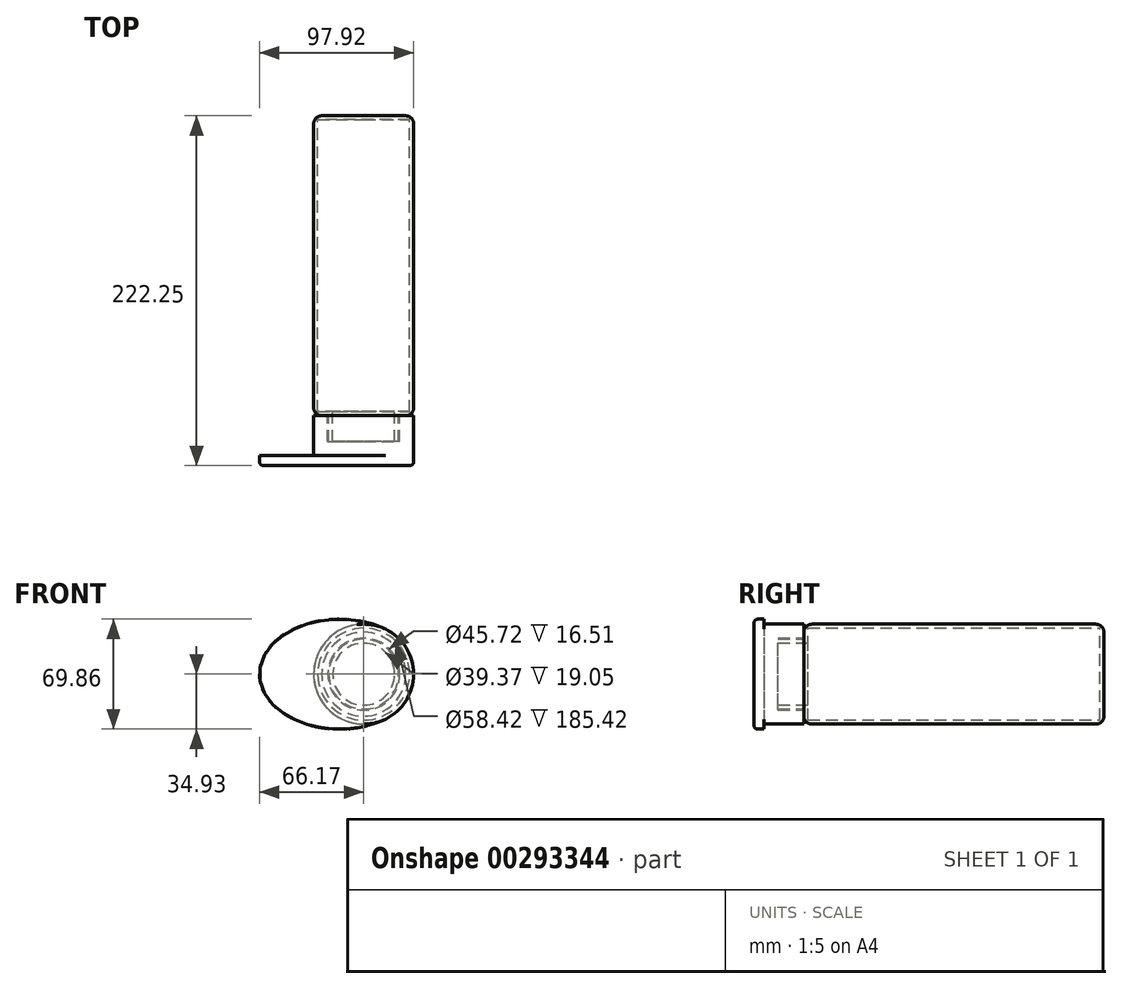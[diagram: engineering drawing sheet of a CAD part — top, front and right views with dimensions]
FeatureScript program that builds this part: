
annotation { "Feature Type Name" : "Feature", "Feature Type Description" : "" }
export const myFeature = defineFeature(function(context is Context, id is Id, definition is map)
    precondition{}
    {
        {
            var Q0;
            Q0=qCreatedBy(makeId("Front.planeOp"),FACE);
            var sketch = newSketch(context, id + "F0", { "sketchPlane" : qUnion([Q0])});
            skCircle(sketch, "E0", {"center": v(0, 0) * mm, "radius": 31.75 * mm});
            skSolve(sketch);
        }
        {
            var Q0;
            Q0 = qSketchRegion(id + "F0", true);
            extrude(context, id + "F1", {"entities" : qUnion([Q0]), "depth" : 190.5 * mm});
        }
        {
            var Q0;
            Q0=makeQuery(id+"F1.opExtrude","CAP_FACE",FACE,{"disambiguationData":[OSD([sQuery(id+"F0.wireOp",EDGE,"E0")])],"isStart":false});
            var sketch = newSketch(context, id + "F2", { "sketchPlane" : qUnion([Q0])});
            skCircle(sketch, "E1", {"center": v(0, 0) * mm, "radius": 22.23 * mm});
            skSolve(sketch);
        }
        {
            var Q0;
            Q0 = qSketchRegion(id + "F2", true);
            extrude(context, id + "F3", {"entities" : qUnion([Q0]), "operationType" : NewBodyOperationType.ADD, "depth" : 25.4 * mm});
        }
        {
            var Q0;
            Q0=makeQuery(id+"F3.opExtrude","CAP_FACE",FACE,{"disambiguationData":[OSD([sQuery(id+"F2.wireOp",EDGE,"E1")])],"isStart":false});
            shell(context, id + "F4", {"entities" : qUnion([Q0]), "thickness" : 2.54 * mm});
        }
        {
            var Q0;
            Q0=makeQuery(id+"F1.opExtrude","CAP_EDGE",EDGE,{"disambiguationData":[OSD([sQuery(id+"F0.wireOp",EDGE,"E0")])],"isStart":false});
            var Q1;
            Q1=makeQuery(id+"F1.opExtrude","CAP_EDGE",EDGE,{"disambiguationData":[OSD([sQuery(id+"F0.wireOp",EDGE,"E0")])],"isStart":true});
            fillet(context, id + "F5", {"entities" : qUnion([Q0, Q1]), "radius" : 5.08 * mm, "tangentPropagation" : true, "allowEdgeOverflow" : false});
        }
        {
            var Q0;
            Q0=makeQuery(id+"F1.opExtrude","CAP_FACE",FACE,{"disambiguationData":[OSD([sQuery(id+"F0.wireOp",EDGE,"E0")])],"isStart":false});
            var sketch = newSketch(context, id + "F6", { "sketchPlane" : qUnion([Q0])});
            skCircle(sketch, "E2", {"center": v(0, 0) * mm, "radius": 31.75 * mm});
            skSolve(sketch);
        }
        {
            var Q0;
            Q0 = qSketchRegion(id + "F6", true);
            extrude(context, id + "F7", {"entities" : qUnion([Q0]), "depth" : 25.4 * mm});
        }
        {
            var Q0;
            Q0=makeQuery(id+"F7.opExtrude","CAP_FACE",FACE,{"disambiguationData":[OSD([sQuery(id+"F6.wireOp",EDGE,"E2")])],"isStart":true});
            shell(context, id + "F8", {"entities" : qUnion([Q0]), "thickness" : 8.9 * mm});
        }
        {
            var Q0;
            Q0=makeQuery(id+"F7.opExtrude","CAP_FACE",FACE,{"disambiguationData":[OSD([sQuery(id+"F6.wireOp",EDGE,"E2")])],"isStart":false});
            var sketch = newSketch(context, id + "F9", { "sketchPlane" : qUnion([Q0])});
            skArc(sketch, "E3", {"start": v(13.77, -28.6) * mm, "mid": v(31.75, 0) * mm, "end": v(13.77, 28.6) * mm});
            skEllipticalArc(sketch, "E4", {});
            skFitSpline(sketch, "E5.0", {"points": [v(27.78, -1.18) * mm, v(27.83, 0) * mm, v(27.78, 1.18) * mm, v(27.61, 2.76) * mm, v(27.19, 4.72) * mm, v(26.33, 7.08) * mm, v(25.1, 9.44) * mm, v(23.5, 11.78) * mm, v(21.5, 14.08) * mm, v(19.5, 15.94) * mm, v(17.7, 17.38) * mm, v(16.25, 18.42) * mm, v(14.71, 19.43) * mm, v(12.56, 20.7) * mm, v(9.68, 22.17) * mm, v(5.97, 23.7) * mm, v(2.02, 24.98) * mm, v(-2.13, 26) * mm, v(-6.43, 26.75) * mm, v(-10.12, 27.13) * mm, v(-13.1, 27.28) * mm, v(-15.37, 27.32) * mm, v(-17.63, 27.28) * mm, v(-20.62, 27.13) * mm, v(-24.3, 26.75) * mm, v(-28.61, 26) * mm, v(-32.75, 24.98) * mm, v(-36.7, 23.7) * mm, v(-40.42, 22.17) * mm, v(-43.3, 20.7) * mm, v(-45.45, 19.43) * mm, v(-46.99, 18.42) * mm, v(-48.44, 17.38) * mm, v(-50.23, 15.94) * mm, v(-52.23, 14.08) * mm, v(-54.23, 11.78) * mm, v(-55.84, 9.44) * mm, v(-57.06, 7.08) * mm, v(-57.92, 4.72) * mm, v(-58.35, 2.76) * mm, v(-58.52, 1.18) * mm, v(-58.56, 0) * mm, v(-58.52, -1.18) * mm, v(-58.35, -2.76) * mm, v(-57.92, -4.72) * mm, v(-57.06, -7.08) * mm, v(-55.84, -9.44) * mm, v(-54.23, -11.78) * mm, v(-52.23, -14.08) * mm, v(-50.23, -15.94) * mm, v(-48.44, -17.38) * mm, v(-46.99, -18.42) * mm, v(-45.45, -19.43) * mm, v(-43.3, -20.7) * mm, v(-40.42, -22.17) * mm, v(-36.7, -23.7) * mm, v(-32.75, -24.98) * mm, v(-28.61, -26) * mm, v(-24.3, -26.75) * mm, v(-20.62, -27.13) * mm, v(-17.63, -27.28) * mm, v(-15.37, -27.32) * mm, v(-13.1, -27.28) * mm, v(-10.12, -27.13) * mm, v(-6.43, -26.75) * mm, v(-2.13, -26) * mm, v(2.02, -24.98) * mm, v(5.97, -23.7) * mm, v(9.68, -22.17) * mm, v(12.56, -20.7) * mm, v(14.71, -19.43) * mm, v(16.25, -18.42) * mm, v(17.7, -17.38) * mm, v(19.5, -15.94) * mm, v(21.5, -14.08) * mm, v(23.5, -11.78) * mm, v(25.1, -9.44) * mm, v(26.33, -7.08) * mm, v(27.19, -4.72) * mm, v(27.61, -2.76) * mm, v(27.78, -1.18) * mm, v(27.83, 0) * mm, v(27.78, 1.18) * mm]});
            skArc(sketch, "E6.trimOffspring", {"start": v(-16.21, 27.3) * mm, "mid": v(-31.75, 0) * mm, "end": v(-16.21, -27.3) * mm});
            const initialGuessF9  = {"E4": [-0.015368361800188331, 0, 1, 0, 0.0508, 0.034925, 0.959804088864332, 5.32338121831523]};
            skSetInitialGuess(sketch, initialGuessF9);
            skSolve(sketch);
        }
        {
            var Q0;
            Q0 = qSketchRegion(id + "F9", true);
            extrude(context, id + "F10", {"entities" : qUnion([Q0]), "operationType" : NewBodyOperationType.ADD, "depth" : 6.35 * mm});
        }
        {
            var Q0;
            Q0=makeQuery(id+"F10.opExtrude","CAP_EDGE",EDGE,{"disambiguationData":[OSD([sQuery(id+"F9.wireOp",EDGE,"E4")])],"isStart":false});
            var Q1;
            Q1=makeQuery(id+"F10.opExtrude","CAP_EDGE",EDGE,{"disambiguationData":[OSD([sQuery(id+"F9.wireOp",EDGE,"E3")])],"isStart":false});
            var Q2;
            Q2=makeQuery(id+"F10.opExtrude","CAP_EDGE",EDGE,{"disambiguationData":[OSD([sQuery(id+"F9.wireOp",EDGE,"E6.trimOffspring")])],"isStart":false});
            var Q3;
            Q3=makeQuery(id+"F10.opExtrude","CAP_EDGE",EDGE,{"disambiguationData":[OSD([sQuery(id+"F9.wireOp",EDGE,"E5.0")])],"isStart":false});
            fillet(context, id + "F11", {"entities" : qUnion([Q0, Q1, Q2, Q3]), "radius" : 2.54 * mm, "tangentPropagation" : true, "allowEdgeOverflow" : false});
        }
    });
